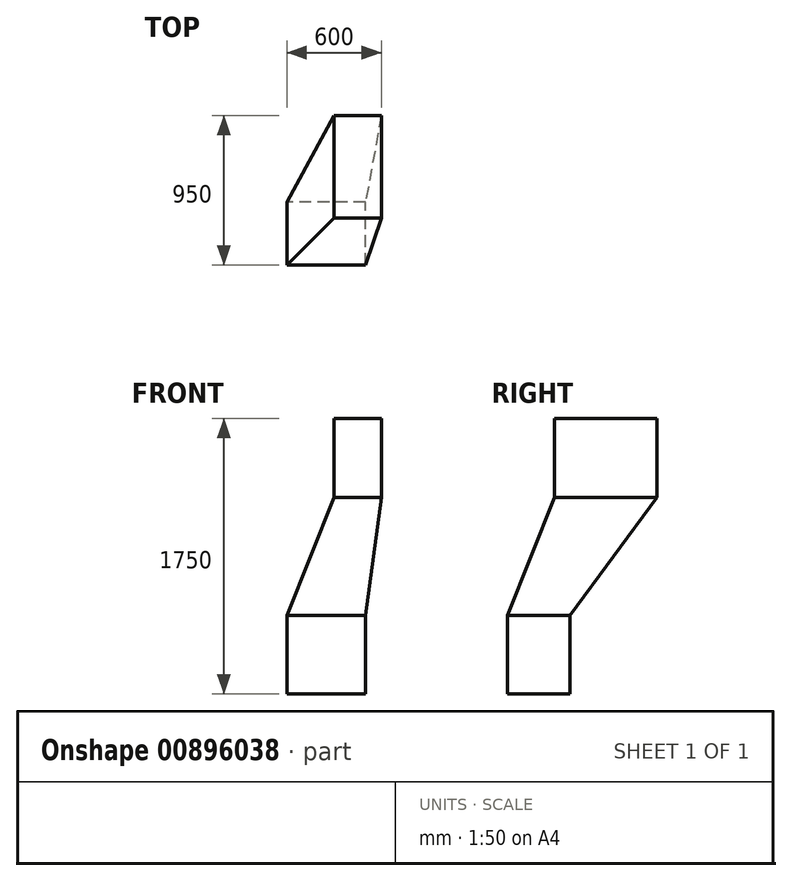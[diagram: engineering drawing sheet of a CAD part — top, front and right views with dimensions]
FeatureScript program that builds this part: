
annotation { "Feature Type Name" : "Feature", "Feature Type Description" : "" }
export const myFeature = defineFeature(function(context is Context, id is Id, definition is map)
    precondition{}
    {
        {
            var Q0;
            Q0=qCreatedBy(makeId("Top.planeOp"),FACE);
            var sketch = newSketch(context, id + "F0", { "sketchPlane" : qUnion([Q0])});
            skLineSegment(sketch, "E0.bottom", {"start": v(250, -200) * mm, "end": v(-250, -200) * mm});
            skLineSegment(sketch, "E0.top", {"start": v(250, 200) * mm, "end": v(-250, 200) * mm});
            skLineSegment(sketch, "E0.left", {"start": v(250, -200) * mm, "end": v(250, 200) * mm});
            skLineSegment(sketch, "E0.right", {"start": v(-250, -200) * mm, "end": v(-250, 200) * mm});
            skPoint(sketch, "E0.middle", {"position": v(0, 0) * mm});
            skSolve(sketch);
        }
        {
            var Q0;
            Q0=makeQuery(id+"F0.imprint","IMPRINT",FACE,{"disambiguationData":[TD([[makeQuery(id+"F0.imprint","IMPRINT",EDGE,{"derivedFrom":sQuery(id+"F0.wireOp",EDGE,"E0.bottom")}),-1.0]])]});
            cPlane(context, id + "F1", {"entities" : qUnion([Q0]), "cplaneType" : CPlaneType.OFFSET, "offset" : 750 * mm, "width" : 150 * mm, "height" : 150 * mm});
        }
        {
            var Q0;
            Q0=qCreatedBy(id+"F1.planeOp",FACE);
            var sketch = newSketch(context, id + "F2", { "sketchPlane" : qUnion([Q0])});
            skLineSegment(sketch, "E1.bottom", {"start": v(50, 750) * mm, "end": v(350, 750) * mm});
            skLineSegment(sketch, "E1.top", {"start": v(50, 100) * mm, "end": v(350, 100) * mm});
            skLineSegment(sketch, "E1.left", {"start": v(50, 750) * mm, "end": v(50, 100) * mm});
            skLineSegment(sketch, "E1.right", {"start": v(350, 750) * mm, "end": v(350, 100) * mm});
            skLineSegment(sketch, "E2.0", {"start": v(-250, -200) * mm, "end": v(-250, 200) * mm});
            skLineSegment(sketch, "E3.0", {"start": v(250, -200) * mm, "end": v(-250, -200) * mm});
            skSolve(sketch);
        }
        {
            var Q0;
            Q0=makeQuery(id+"F2.imprint","IMPRINT",FACE,{"disambiguationData":[TD([[makeQuery(id+"F2.imprint","IMPRINT",EDGE,{"derivedFrom":sQuery(id+"F2.wireOp",EDGE,"E1.bottom")}),-1.0]])]});
            var Q1;
            Q1=makeQuery(id+"F0.imprint","IMPRINT",FACE,{"disambiguationData":[TD([[makeQuery(id+"F0.imprint","IMPRINT",EDGE,{"derivedFrom":sQuery(id+"F0.wireOp",EDGE,"E0.bottom")}),-1.0]])]});
            loft(context, id + "F3", {"sheetProfilesArray" : [{ "sheetProfileEntities" : qUnion([Q0]) }, { "sheetProfileEntities" : qUnion([Q1]) }]});
        }
        {
            var Q0;
            Q0=makeQuery(id+"F3.opLoft","CAP_FACE",FACE,{"disambiguationData":[OSD([makeQuery(id+"F0.imprint","IMPRINT",FACE,{"disambiguationData":[TD([[makeQuery(id+"F0.imprint","IMPRINT",EDGE,{"derivedFrom":sQuery(id+"F0.wireOp",EDGE,"E0.bottom")}),-1.0]])]})])],"isStart":true});
            extrude(context, id + "F4", {"entities" : qUnion([Q0]), "depth" : 500 * mm, "offsetDistance" : 25 * mm});
        }
        {
            var Q0;
            Q0=makeQuery(id+"F3.opLoft","CAP_FACE",FACE,{"disambiguationData":[OSD([makeQuery(id+"F2.imprint","IMPRINT",FACE,{"disambiguationData":[TD([[makeQuery(id+"F2.imprint","IMPRINT",EDGE,{"derivedFrom":sQuery(id+"F2.wireOp",EDGE,"E1.bottom")}),-1.0]])]})])],"isStart":true});
            extrude(context, id + "F5", {"entities" : qUnion([Q0]), "depth" : 500 * mm, "offsetDistance" : 25 * mm});
        }
    });
